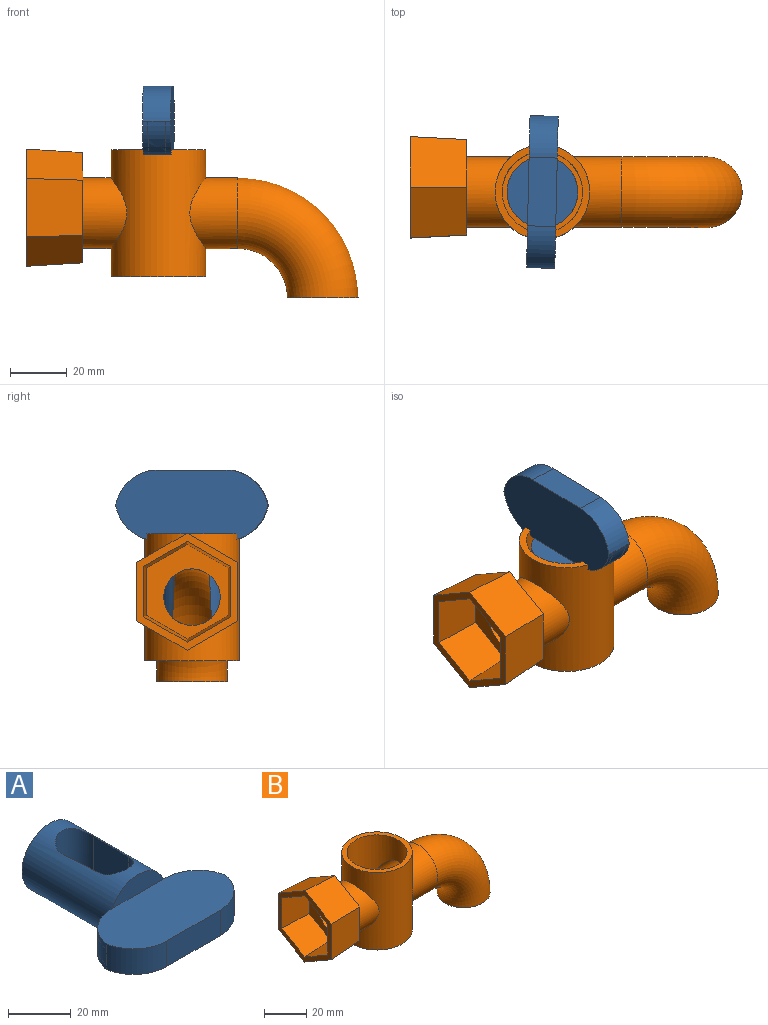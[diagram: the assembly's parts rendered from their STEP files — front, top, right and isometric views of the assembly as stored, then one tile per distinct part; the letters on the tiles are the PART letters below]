
ASSEMBLY  parts=2 mates=1
PART A: 23 faces, bbox 54.4x65.2x25.2 mm
  f0: plane 1.88x0.65mm, normal (0,1,0), area 0.6mm2, adj f3,f13,f19
  f1: plane 1.88x0.65mm, normal (0,1,0), area 0.6mm2, adj f3,f12,f18
  f2: plane 22.92x7.51mm, normal (0,-1,0), area 124.1mm2, adj f3,f13
  f3: cylinder r=12.5mm len=40mm, axis (0,1,0), area 2383.6mm2, adj f0,f1,f2,f4,f5,f6,f7,f8
  f4: plane 22.92x7.51mm, normal (0,-1,0), area 124.1mm2, adj f3,f12
  f5: plane 25x25mm, normal (0,1,0), area 490.9mm2, adj f3
  f6: plane 21.69x16.74mm, normal (-1,0.04,0), area 349.3mm2, adj f3,f7,f9
  f7: cylinder r=7.08mm len=20.63mm, axis (0,0,1), area 467.3mm2, adj f3,f6,f8
  f8: plane 21.68x16.16mm, normal (1,0.04,0), area 337.5mm2, adj f3,f7,f9
  f9: cylinder r=6.37mm len=21.51mm, axis (0,0,1), area 419mm2, adj f3,f6,f8
  f10: plane 1.88x0.65mm, normal (0,1,0), area 0.6mm2, adj f3,f13,f15
  f11: plane 1.88x0.65mm, normal (0,1,0), area 0.6mm2, adj f3,f12,f22
  f12: plane 53.79x25mm, normal (0,0,1), area 1162.9mm2, adj f1,f4,f11,f14,f16,f18,f20,f22
  f13: plane 53.79x25mm, normal (0,0,-1), area 1162.9mm2, adj f0,f2,f10,f14,f15,f16,f19,f20
  f14: plane 24.21x9.98mm, normal (0,-1,0), area 241.7mm2, adj f12,f13,f16,f20
  f15: cylinder r=15mm len=14.79mm, axis (0,0,1), area 39.5mm2, adj f10,f13,f16,f17
  f16: cylinder r=15mm len=14.79mm, axis (0,0,-1), area 210.1mm2, adj f12,f13,f14,f15,f17,f18
  f17: bspline ~15.34x15.31mm, area 129.5mm2, adj f3,f15,f16,f18
  f18: cylinder r=15mm len=14.79mm, axis (0,0,1), area 39.5mm2, adj f1,f12,f16,f17
  f19: cylinder r=15mm len=14.79mm, axis (0,0,-1), area 39.5mm2, adj f0,f13,f20,f21
  f20: cylinder r=15mm len=14.79mm, axis (0,0,1), area 210.1mm2, adj f12,f13,f14,f19,f21,f22
  f21: bspline ~15.34x15.31mm, area 129.5mm2, adj f3,f19,f20,f22
  f22: cylinder r=15mm len=14.79mm, axis (0,0,-1), area 39.5mm2, adj f11,f12,f20,f21
PART B: 27 faces, bbox 121x36.4x52.6 mm
  f0: cylinder r=12.5mm len=25mm, axis (1,0,0), area 1105.6mm2, adj f2,f3
  f1: plane 25x25mm, normal (0,0,-1), area 176.7mm2, adj f2,f16
  f2: torus R=30mm, axis (0,1,0), area 3701.1mm2, adj f0,f1
  f3: cylinder r=16.74mm len=45mm, axis (0,0,-1), area 3661.5mm2, adj f0,f4,f5,f6
  f4: plane 33.48x33.48mm, normal (0,0,1), area 243.3mm2, adj f3,f17
  f5: plane 33.48x33.48mm, normal (0,0,-1), area 880.2mm2, adj f3
  f6: cylinder r=12.5mm len=25mm, axis (1,0,0), area 1003.1mm2, adj f3,f14
  f7: plane 20x17.94mm, normal (0.05,0.5,-0.86), area 402.7mm2, adj f8,f12,f13,f14
  f8: plane 20.71x20mm, normal (0.05,1,0), area 402.7mm2, adj f7,f9,f13,f14
  f9: plane 20x17.94mm, normal (0.05,0.5,0.86), area 402.7mm2, adj f8,f10,f13,f14
  f10: plane 20x17.94mm, normal (0.05,-0.5,0.86), area 402.7mm2, adj f9,f11,f13,f14
  f11: plane 20.71x20mm, normal (0.05,-1,0), area 402.7mm2, adj f10,f12,f13,f14
  f12: plane 20x17.94mm, normal (0.05,-0.5,-0.86), area 402.7mm2, adj f7,f11,f13,f14
  f13: plane 41.42x35.87mm, normal (-1,0,0), area 289.4mm2, adj f7,f8,f9,f10,f11,f12,f20,f21
  f14: plane 39x33.77mm, normal (1,0,0), area 497mm2, adj f6,f7,f8,f9,f10,f11,f12
  f15: cylinder r=10mm len=20mm, axis (1,0,0), area 997.7mm2, adj f16,f17
  f16: torus R=30mm, axis (0,1,0), area 2960.9mm2, adj f1,f15
  f17: cylinder r=14.24mm len=42.5mm, axis (0,0,-1), area 3125.1mm2, adj f4,f15,f18,f19
  f18: plane 28.48x28.48mm, normal (0,0,1), area 636.9mm2, adj f17
  f19: cylinder r=10mm len=20mm, axis (1,0,0), area 1072.7mm2, adj f17,f26
  f20: plane 17.5x15.43mm, normal (-0.05,-0.5,0.86), area 303mm2, adj f13,f21,f25,f26
  f21: plane 17.82x17.5mm, normal (-0.05,-1,0), area 303mm2, adj f13,f20,f22,f26
  f22: plane 17.5x15.43mm, normal (-0.05,-0.5,-0.86), area 303mm2, adj f13,f21,f23,f26
  f23: plane 17.5x15.43mm, normal (-0.05,0.5,-0.86), area 303mm2, adj f13,f22,f24,f26
  f24: plane 17.82x17.5mm, normal (-0.05,1,0), area 303mm2, adj f13,f23,f25,f26
  f25: plane 17.5x15.43mm, normal (-0.05,0.5,0.86), area 303mm2, adj f13,f20,f24,f26
  f26: plane 33.52x29.03mm, normal (-1,0,0), area 415.7mm2, adj f19,f20,f21,f22,f23,f24,f25
PLACE A rot(axis=(-0.59,-0.57,0.57),119.2deg) t=(26.85,0,-20)mm
PLACE B at identity fixed
MATE revolute A.f3 <-> B.f3  axis (0,0,-1) through (26.85,0,-20)mm
